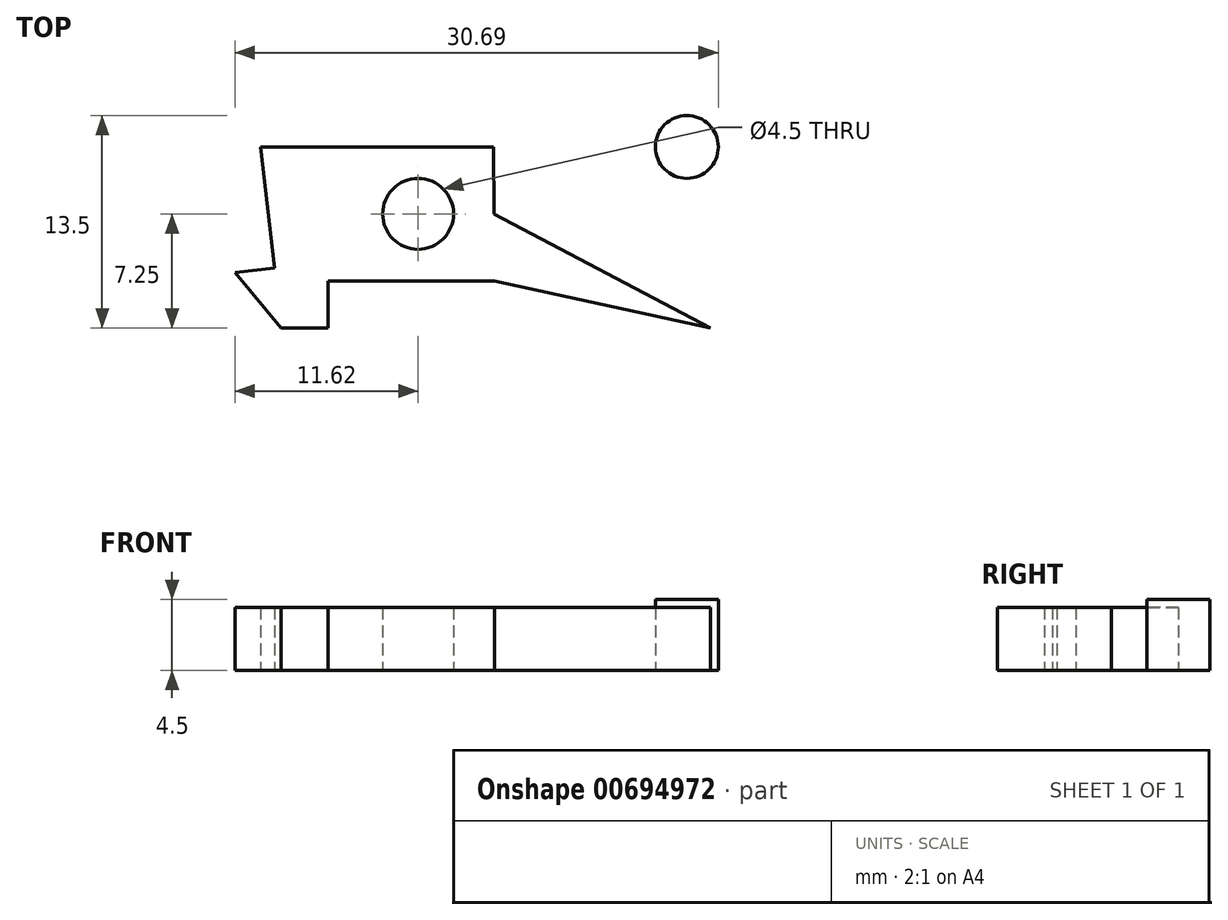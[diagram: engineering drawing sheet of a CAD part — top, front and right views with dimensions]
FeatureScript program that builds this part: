
annotation { "Feature Type Name" : "Feature", "Feature Type Description" : "" }
export const myFeature = defineFeature(function(context is Context, id is Id, definition is map)
    precondition{}
    {
        {
            var Q0;
            Q0=qCreatedBy(makeId("Top.planeOp"),FACE);
            var sketch = newSketch(context, id + "F0", { "sketchPlane" : qUnion([Q0])});
            skPoint(sketch, "E0.middle", {"position": v(0, 0) * mm});
            skCircle(sketch, "E1", {"center": v(0, 0) * mm, "radius": 2.25 * mm});
            skLineSegment(sketch, "E2", {"start": v(-5.7, -7.25) * mm, "end": v(-5.7, -4.25) * mm});
            skLineSegment(sketch, "E3", {"start": v(4.8, 4.25) * mm, "end": v(4.87, -4.25) * mm});
            skLineSegment(sketch, "E4", {"start": v(4.83, 0) * mm, "end": v(18.56, -7.25) * mm});
            skLineSegment(sketch, "E5", {"start": v(4.87, -4.25) * mm, "end": v(18.56, -7.25) * mm});
            skLineSegment(sketch, "E6", {"start": v(-5.7, -7.25) * mm, "end": v(-8.7, -7.25) * mm});
            skLineSegment(sketch, "E7", {"start": v(-8.7, -7.25) * mm, "end": v(-10, 4.25) * mm});
            skLineSegment(sketch, "E8", {"start": v(-5.7, -4.25) * mm, "end": v(4.87, -4.25) * mm});
            skLineSegment(sketch, "E9", {"start": v(-10, 4.25) * mm, "end": v(4.8, 4.25) * mm});
            skLineSegment(sketch, "E10", {"start": v(-8.7, -7.25) * mm, "end": v(-11.62, -3.73) * mm});
            skLineSegment(sketch, "E11", {"start": v(-11.62, -3.73) * mm, "end": v(-9.13, -3.45) * mm});
            skCircle(sketch, "E12", {"center": v(17.07, 4.25) * mm, "radius": 2 * mm});
            skSolve(sketch);
        }
        {
            var Q0;
            Q0=makeQuery(id+"F0.imprint","IMPRINT",FACE,{"disambiguationData":[TD([[makeQuery(id+"F0.imprint","IMPRINT",EDGE,{"derivedFrom":sQuery(id+"F0.wireOp",EDGE,"E1")}),-1.0]])]});
            var Q1;
            {var subQ0=sQuery(id+"F0.wireOp",EDGE,"E2");Q1=makeQuery(id+"F0.imprint","IMPRINT",FACE,{"disambiguationData":[TD([[makeQuery(id+"F0.imprint","IMPRINT",EDGE,{"derivedFrom":subQ0}),1.0]])]});}
            var Q2;
            {var subQ0=sQuery(id+"F0.wireOp",EDGE,"E0.right");var subQ1=sQuery(id+"F0.wireOp",EDGE,"E0.top");var subQ2=makeQuery(id+"F0.imprint","INTERSECT",VERTEX,{"derivedFrom":[subQ1,subQ0]});Q2=makeQuery(id+"F0.imprint","IMPRINT",FACE,{"disambiguationData":[TD([[makeQuery(id+"F0.imprint","IMPRINT",EDGE,{"disambiguationData":[TD([[subQ2,1.0]])],"derivedFrom":subQ0}),-1.0]])]});}
            var Q3;
            {var subQ3=sQuery(id+"F0.wireOp",EDGE,"E5");Q3=makeQuery(id+"F0.imprint","IMPRINT",FACE,{"disambiguationData":[TD([[makeQuery(id+"F0.imprint","IMPRINT",EDGE,{"derivedFrom":subQ3}),1.0]])]});}
            var Q4;
            {var subQ0=sQuery(id+"F0.wireOp",EDGE,"E10");Q4=makeQuery(id+"F0.imprint","IMPRINT",FACE,{"disambiguationData":[TD([[makeQuery(id+"F0.imprint","IMPRINT",EDGE,{"derivedFrom":subQ0}),-1.0]])]});}
            extrude(context, id + "F1", {"entities" : qUnion([Q0, Q1, Q2, Q3, Q4]), "depth" : 4 * mm, "offsetDistance" : 25 * mm});
        }
        {
            var Q0;
            Q0=makeQuery(id+"F0.imprint","IMPRINT",FACE,{"disambiguationData":[TD([[makeQuery(id+"F0.imprint","IMPRINT",EDGE,{"derivedFrom":sQuery(id+"F0.wireOp",EDGE,"E12")}),1.0]])]});
            extrude(context, id + "F2", {"entities" : qUnion([Q0]), "depth" : 4.5 * mm, "offsetDistance" : 25 * mm});
        }
    });
